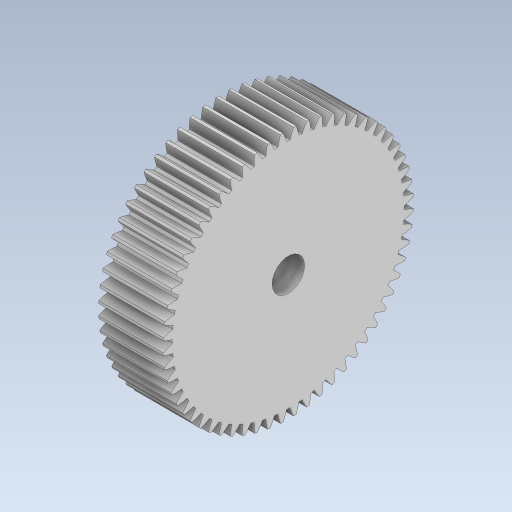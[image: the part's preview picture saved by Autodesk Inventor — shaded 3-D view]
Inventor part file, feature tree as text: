
AUTODESK INVENTOR PART (.ipt)
format: ipt  version: 2023 (Build 270158000, 158)  size: 467,456 bytes
history: native  units: in
note: dims shown in document units (in); Inventor stores cm internally (conversion verified against a paired STEP export)
features: extrude x2, sketch x2, other x1
ambient origin geometry x8: Origin, YZ Plane, XZ Plane, XY Plane, X Axis, Y Axis, Z Axis, Center Point
bodies: Solid1 (feature_tree)
feature tree (5):
  extrude  "Extrusion1"  TaperAngle=0.0deg  [1 undecoded]
  extrude  "Extrusion2"  TaperAngle=0.0deg  [1 undecoded]
  sketch  "Sketch1"  dims[d0=0.5in d1=0.0in d2=0.0in]
  sketch  "Sketch2"  dims[d3=0.25in d4=0.0in d5=0.0in]
  other  "TeethCuts"
note: 2 required parameter values undecoded (feature->parameter linkage not recoverable at this tier; creation-order binding heuristic only, values carry confidence <= 0.55)
